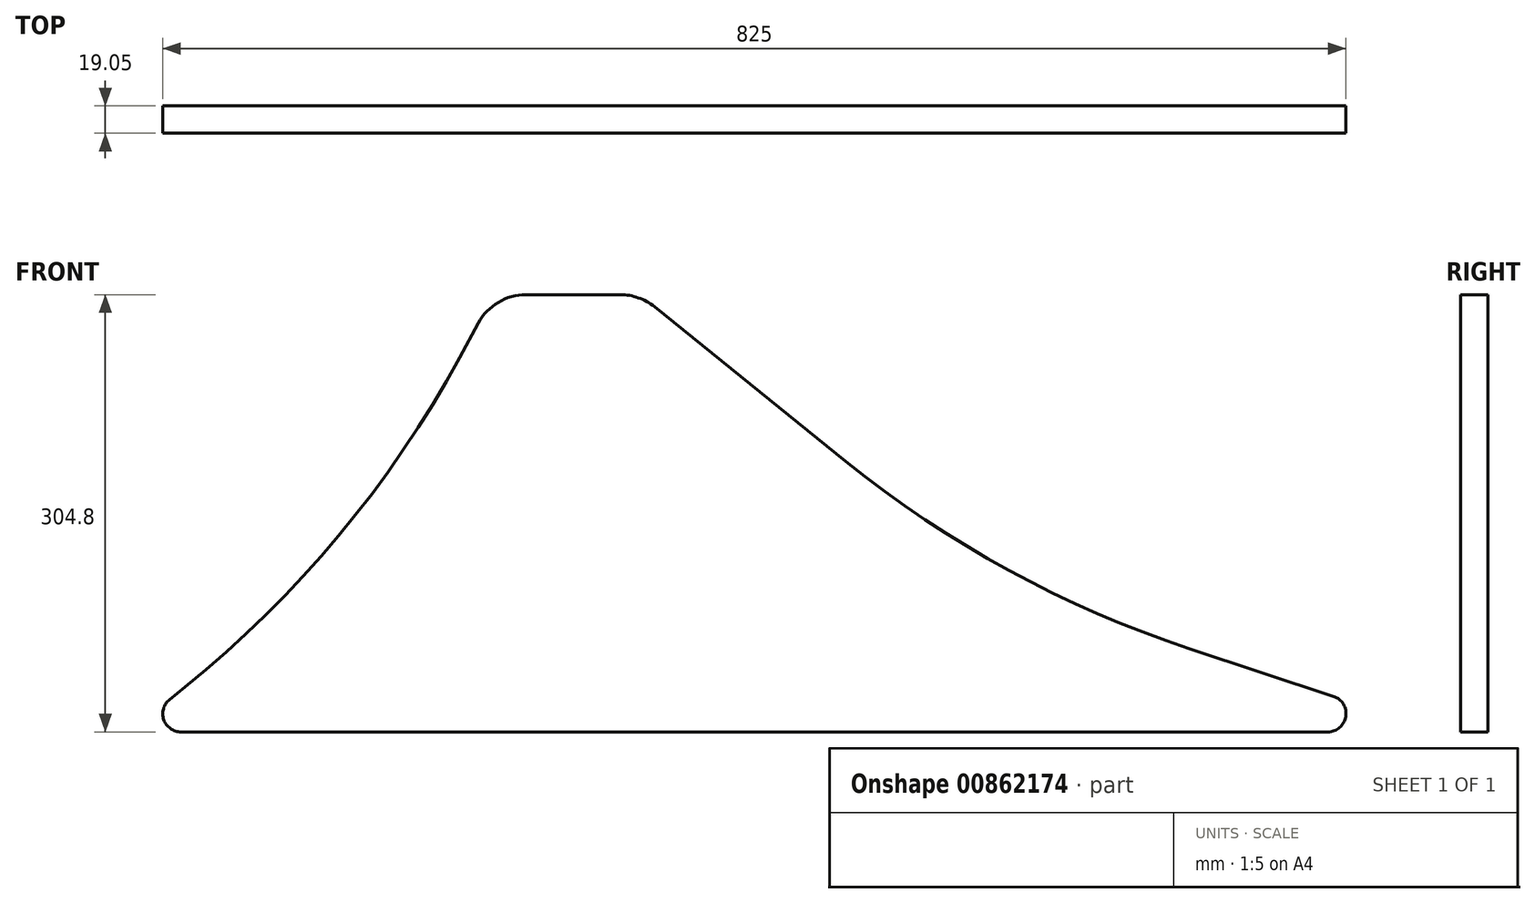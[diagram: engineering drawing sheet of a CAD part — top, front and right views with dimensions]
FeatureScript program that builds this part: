
annotation { "Feature Type Name" : "Feature", "Feature Type Description" : "" }
export const myFeature = defineFeature(function(context is Context, id is Id, definition is map)
    precondition{}
    {
        {
            var Q0;
            Q0=qCreatedBy(makeId("Front.planeOp"),FACE);
            var sketch = newSketch(context, id + "F0", { "sketchPlane" : qUnion([Q0])});
            skLineSegment(sketch, "E0", {"start": v(0, 0) * mm, "end": v(157.48, 127) * mm});
            skLineSegment(sketch, "E1", {"start": v(157.48, 127) * mm, "end": v(254, 304.8) * mm});
            skLineSegment(sketch, "E2", {"start": v(254, 304.8) * mm, "end": v(355.6, 304.8) * mm});
            skLineSegment(sketch, "E3", {"start": v(355.6, 304.8) * mm, "end": v(607.3, 101.6) * mm});
            skLineSegment(sketch, "E4", {"start": v(607.3, 101.6) * mm, "end": v(914.4, 0) * mm});
            skLineSegment(sketch, "E5", {"start": v(914.4, 0) * mm, "end": v(0, 0) * mm});
            skSolve(sketch);
        }
        {
            var Q0;
            Q0=makeQuery(id+"F0.imprint","IMPRINT",FACE,{"disambiguationData":[TD([[makeQuery(id+"F0.imprint","IMPRINT",EDGE,{"derivedFrom":sQuery(id+"F0.wireOp",EDGE,"E0")}),-1.0]])]});
            extrude(context, id + "F1", {"entities" : qUnion([Q0]), "depth" : 19.05 * mm, "offsetDistance" : 25.4 * mm});
        }
        {
            var Q0;
            Q0=makeQuery(id+"F1.opExtrude","SWEPT_EDGE",EDGE,{"disambiguationData":[OSD([sQuery(id+"F0.wireOp",EDGE,"E0"),sQuery(id+"F0.wireOp",EDGE,"E1")])]});
            var Q1;
            Q1=makeQuery(id+"F1.opExtrude","SWEPT_EDGE",EDGE,{"disambiguationData":[OSD([sQuery(id+"F0.wireOp",EDGE,"E3"),sQuery(id+"F0.wireOp",EDGE,"E4")])]});
            fillet(context, id + "F2", {"entities" : qUnion([Q0, Q1]), "radius" : 762 * mm, "tangentPropagation" : true, "allowEdgeOverflow" : false});
        }
        {
            var Q0;
            Q0=makeQuery(id+"F1.opExtrude","SWEPT_EDGE",EDGE,{"disambiguationData":[OSD([sQuery(id+"F0.wireOp",EDGE,"E1"),sQuery(id+"F0.wireOp",EDGE,"E2")])]});
            var Q1;
            Q1=makeQuery(id+"F1.opExtrude","SWEPT_EDGE",EDGE,{"disambiguationData":[OSD([sQuery(id+"F0.wireOp",EDGE,"E2"),sQuery(id+"F0.wireOp",EDGE,"E3")])]});
            fillet(context, id + "F3", {"entities" : qUnion([Q0, Q1]), "radius" : 38.1 * mm, "tangentPropagation" : true, "allowEdgeOverflow" : false});
        }
        {
            var Q0;
            Q0=makeQuery(id+"F1.opExtrude","SWEPT_EDGE",EDGE,{"disambiguationData":[OSD([sQuery(id+"F0.wireOp",EDGE,"E4"),sQuery(id+"F0.wireOp",EDGE,"E5")])]});
            var Q1;
            Q1=makeQuery(id+"F1.opExtrude","SWEPT_EDGE",EDGE,{"disambiguationData":[OSD([sQuery(id+"F0.wireOp",EDGE,"E0"),sQuery(id+"F0.wireOp",EDGE,"E5")])]});
            fillet(context, id + "F4", {"entities" : qUnion([Q0, Q1]), "radius" : 12.7 * mm, "tangentPropagation" : true, "allowEdgeOverflow" : false});
        }
    });
